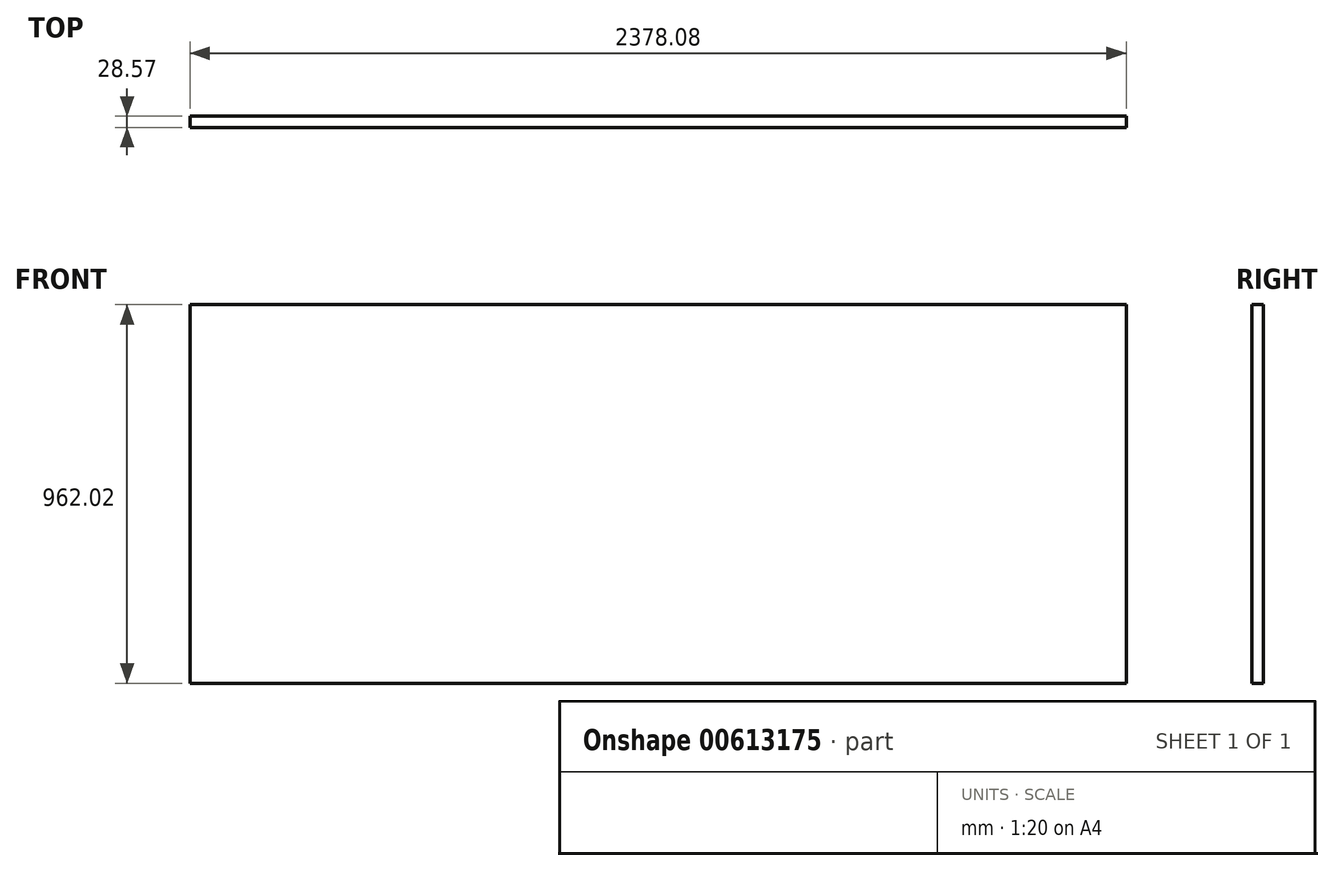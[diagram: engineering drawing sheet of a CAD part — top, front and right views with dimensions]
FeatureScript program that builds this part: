
annotation { "Feature Type Name" : "Feature", "Feature Type Description" : "" }
export const myFeature = defineFeature(function(context is Context, id is Id, definition is map)
    precondition{}
    {
        {
            var Q0;
            Q0=qCreatedBy(makeId("Front.planeOp"),FACE);
            var sketch = newSketch(context, id + "F0", { "sketchPlane" : qUnion([Q0])});
            skLineSegment(sketch, "E0.bottom", {"start": v(1189.04, 481.01) * mm, "end": v(-1189.04, 481.01) * mm});
            skLineSegment(sketch, "E0.top", {"start": v(1189.04, -481.01) * mm, "end": v(-1189.04, -481.01) * mm});
            skLineSegment(sketch, "E0.left", {"start": v(1189.04, 481.01) * mm, "end": v(1189.04, -481.01) * mm});
            skLineSegment(sketch, "E0.right", {"start": v(-1189.04, 481.01) * mm, "end": v(-1189.04, -481.01) * mm});
            skPoint(sketch, "E0.middle", {"position": v(0, 0) * mm});
            skSolve(sketch);
        }
        {
            var Q0;
            Q0=qSketchRegion(id+"F0",true);
            extrude(context, id + "F1", {"entities" : qUnion([Q0]), "depth" : 28.57 * mm, "offsetDistance" : 25.4 * mm});
        }
    });
